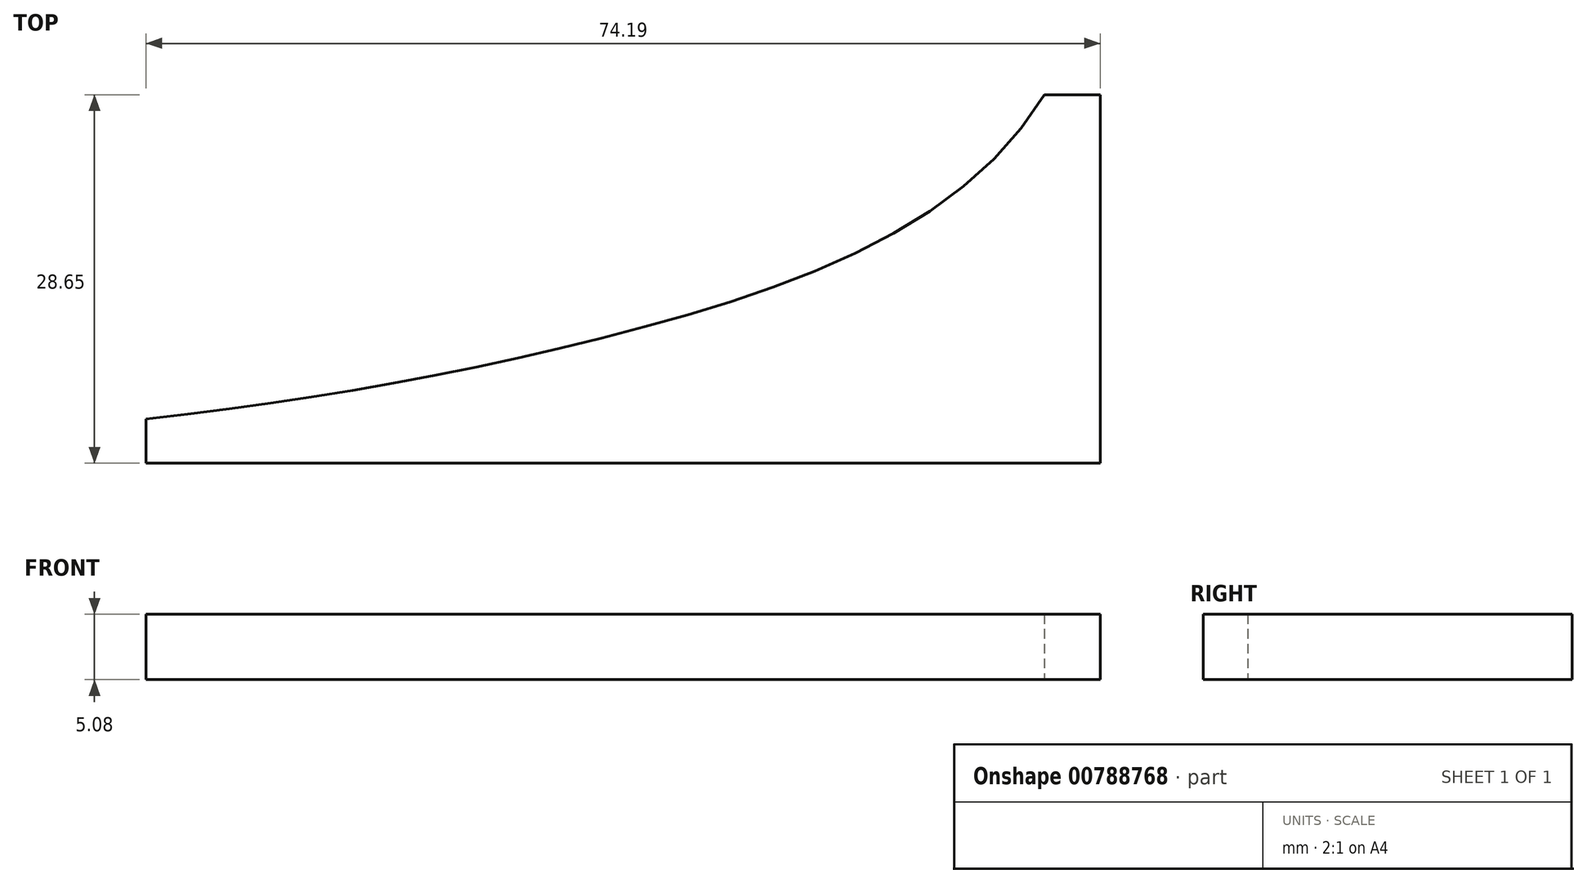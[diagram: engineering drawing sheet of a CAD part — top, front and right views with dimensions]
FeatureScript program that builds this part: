
annotation { "Feature Type Name" : "Feature", "Feature Type Description" : "" }
export const myFeature = defineFeature(function(context is Context, id is Id, definition is map)
    precondition{}
    {
        {
            var Q0;
            Q0=qCreatedBy(makeId("Top.planeOp"),FACE);
            var sketch = newSketch(context, id + "F0", { "sketchPlane" : qUnion([Q0])});
            skLineSegment(sketch, "E0", {"start": v(-174.78, -34.64) * mm, "end": v(-101.74, -34.64) * mm});
            skLineSegment(sketch, "E1", {"start": v(-174.78, -34.64) * mm, "end": v(-174.78, -31.2) * mm});
            skLineSegment(sketch, "E2", {"start": v(-104.97, -5.99) * mm, "end": v(-100.59, -5.99) * mm});
            skLineSegment(sketch, "E3", {"start": v(-100.59, -5.99) * mm, "end": v(-100.59, -34.64) * mm});
            skFitSpline(sketch, "E4", {"points": [v(-104.97, -5.99) * mm, v(-137.65, -24.48) * mm, v(-174.78, -31.2) * mm], "startDerivative": vector(-37.5, -63.4) * mm, "endDerivative": vector(-75.17, -8.35) * mm});
            skLineSegment(sketch, "E5", {"start": v(-101.74, -34.64) * mm, "end": v(-100.59, -34.64) * mm});
            skSolve(sketch);
        }
        {
            var Q0;
            Q0=makeQuery(id+"F0.imprint","IMPRINT",FACE,{"disambiguationData":[TD([[makeQuery(id+"F0.imprint","IMPRINT",EDGE,{"derivedFrom":sQuery(id+"F0.wireOp",EDGE,"E0")}),1.0]])]});
            extrude(context, id + "F1", {"entities" : qUnion([Q0]), "depth" : 5.08 * mm, "offsetDistance" : 25.4 * mm});
        }
    });
